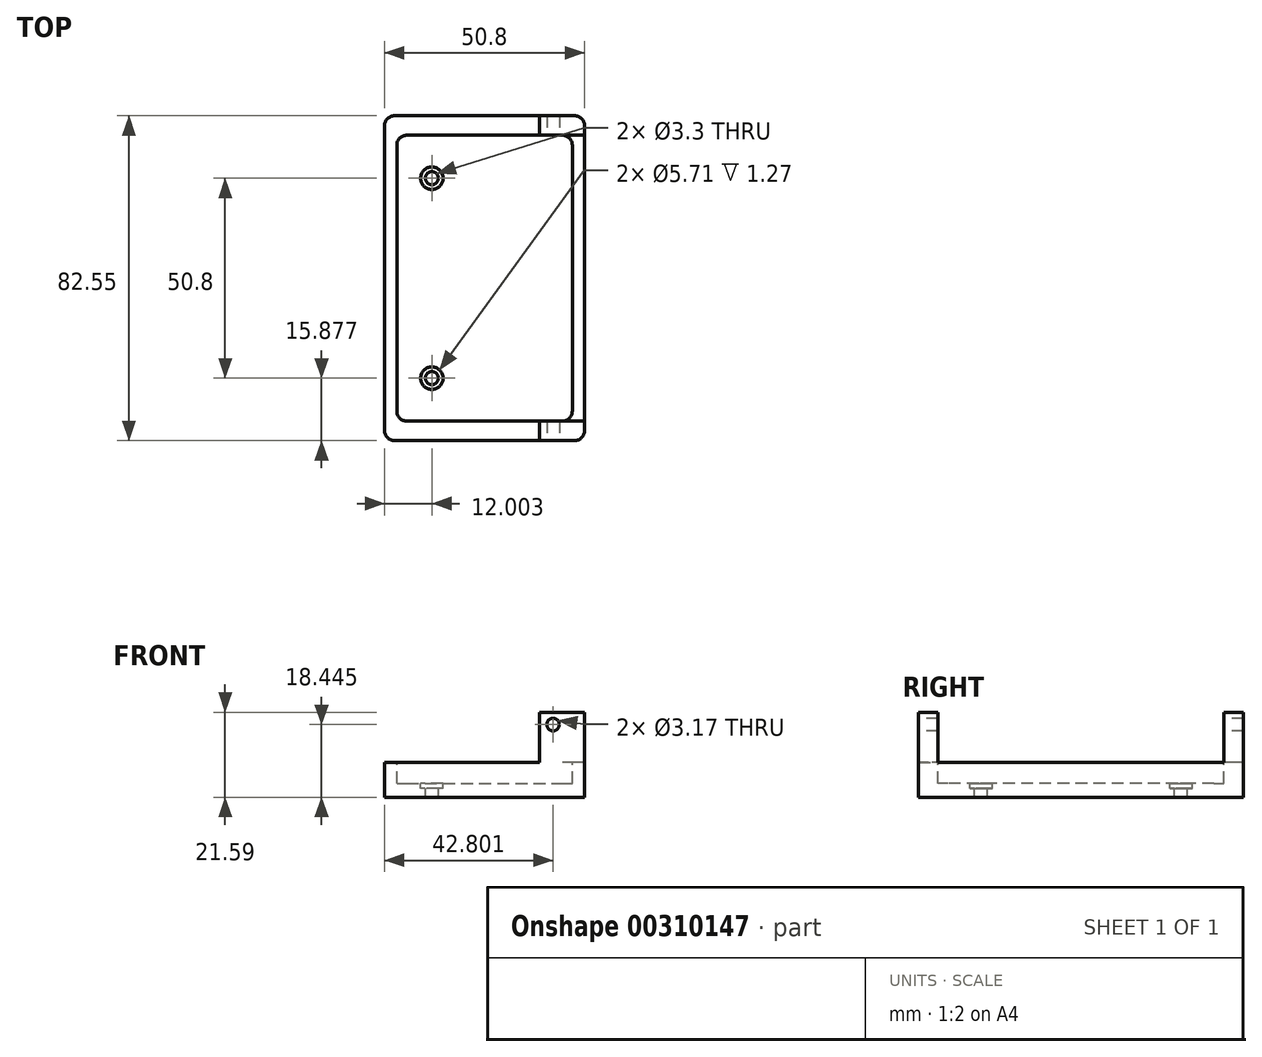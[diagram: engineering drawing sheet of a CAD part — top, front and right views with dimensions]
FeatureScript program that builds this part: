
annotation { "Feature Type Name" : "Feature", "Feature Type Description" : "" }
export const myFeature = defineFeature(function(context is Context, id is Id, definition is map)
    precondition{}
    {
        {
            var Q0;
            Q0=qCreatedBy(makeId("Top.planeOp"),FACE);
            var sketch = newSketch(context, id + "F0", { "sketchPlane" : qUnion([Q0])});
            skLineSegment(sketch, "E0.bottom", {"start": v(-30.54, 37.41) * mm, "end": v(20.26, 37.41) * mm});
            skLineSegment(sketch, "E0.top", {"start": v(-30.54, -45.14) * mm, "end": v(20.26, -45.14) * mm});
            skLineSegment(sketch, "E0.left", {"start": v(-30.54, 37.41) * mm, "end": v(-30.54, -45.14) * mm});
            skLineSegment(sketch, "E0.right", {"start": v(20.26, 37.41) * mm, "end": v(20.26, -45.14) * mm});
            skSolve(sketch);
        }
        {
            var Q0;
            Q0=makeQuery(id+"F0.imprint","IMPRINT",FACE,{"disambiguationData":[TD([[makeQuery(id+"F0.imprint","IMPRINT",EDGE,{"derivedFrom":sQuery(id+"F0.wireOp",EDGE,"E0.bottom")}),-1.0]])]});
            extrude(context, id + "F1", {"entities" : qUnion([Q0]), "depth" : 8.9 * mm});
        }
        {
            var Q0;
            Q0=makeQuery(id+"F1.opExtrude","CAP_FACE",FACE,{"disambiguationData":[OSD([sQuery(id+"F0.wireOp",EDGE,"E0.bottom"),sQuery(id+"F0.wireOp",EDGE,"E0.top"),sQuery(id+"F0.wireOp",EDGE,"E0.left"),sQuery(id+"F0.wireOp",EDGE,"E0.right")])],"isStart":false});
            var sketch = newSketch(context, id + "F2", { "sketchPlane" : qUnion([Q0])});
            skLineSegment(sketch, "E1.bottom", {"start": v(-27.43, 32.46) * mm, "end": v(17.15, 32.46) * mm});
            skLineSegment(sketch, "E1.top", {"start": v(-27.43, -40.19) * mm, "end": v(17.15, -40.19) * mm});
            skLineSegment(sketch, "E1.left", {"start": v(-27.43, 32.46) * mm, "end": v(-27.43, -40.19) * mm});
            skLineSegment(sketch, "E1.right", {"start": v(17.15, 32.46) * mm, "end": v(17.15, -40.19) * mm});
            skSolve(sketch);
        }
        {
            var Q0;
            Q0=makeQuery(id+"F2.imprint","IMPRINT",FACE,{"disambiguationData":[TD([[makeQuery(id+"F2.imprint","IMPRINT",EDGE,{"derivedFrom":sQuery(id+"F2.wireOp",EDGE,"E1.bottom")}),-1.0]])]});
            extrude(context, id + "F3", {"entities" : qUnion([Q0]), "operationType" : NewBodyOperationType.REMOVE, "oppositeDirection" : true, "depth" : 5.33 * mm});
        }
        {
            var Q0;
            Q0=makeQuery(id+"F3.boolean.opBoolean","COPY",EDGE,{"derivedFrom":makeQuery(id+"F3.opExtrude","SWEPT_EDGE",EDGE,{"disambiguationData":[OSD([sQuery(id+"F2.wireOp",EDGE,"E1.bottom"),sQuery(id+"F2.wireOp",EDGE,"E1.left")])]})});
            var Q1;
            Q1=makeQuery(id+"F3.boolean.opBoolean","COPY",EDGE,{"derivedFrom":makeQuery(id+"F3.opExtrude","SWEPT_EDGE",EDGE,{"disambiguationData":[OSD([sQuery(id+"F2.wireOp",EDGE,"E1.bottom"),sQuery(id+"F2.wireOp",EDGE,"E1.right")])]})});
            var Q2;
            Q2=makeQuery(id+"F3.boolean.opBoolean","COPY",EDGE,{"derivedFrom":makeQuery(id+"F3.opExtrude","SWEPT_EDGE",EDGE,{"disambiguationData":[OSD([sQuery(id+"F2.wireOp",EDGE,"E1.top"),sQuery(id+"F2.wireOp",EDGE,"E1.right")])]})});
            var Q3;
            Q3=makeQuery(id+"F3.boolean.opBoolean","COPY",EDGE,{"derivedFrom":makeQuery(id+"F3.opExtrude","SWEPT_EDGE",EDGE,{"disambiguationData":[OSD([sQuery(id+"F2.wireOp",EDGE,"E1.top"),sQuery(id+"F2.wireOp",EDGE,"E1.left")])]})});
            fillet(context, id + "F4", {"entities" : qUnion([Q0, Q1, Q2, Q3]), "radius" : 2.54 * mm, "tangentPropagation" : true, "allowEdgeOverflow" : false});
        }
        {
            var Q0;
            Q0=makeQuery(id+"F3.boolean.opBoolean","COPY",FACE,{"derivedFrom":makeQuery(id+"F3.opExtrude","CAP_FACE",FACE,{"disambiguationData":[OSD([sQuery(id+"F2.wireOp",EDGE,"E1.bottom"),sQuery(id+"F2.wireOp",EDGE,"E1.top"),sQuery(id+"F2.wireOp",EDGE,"E1.left"),sQuery(id+"F2.wireOp",EDGE,"E1.right")])],"isStart":false})});
            var sketch = newSketch(context, id + "F5", { "sketchPlane" : qUnion([Q0])});
            skCircle(sketch, "E2", {"center": v(-18.54, 21.54) * mm, "radius": 1.65 * mm});
            skCircle(sketch, "E3", {"center": v(-18.54, -29.26) * mm, "radius": 1.65 * mm});
            skSolve(sketch);
        }
        {
            var Q0;
            Q0=makeQuery(id+"F5.imprint","IMPRINT",FACE,{"disambiguationData":[TD([[makeQuery(id+"F5.imprint","IMPRINT",EDGE,{"derivedFrom":sQuery(id+"F5.wireOp",EDGE,"E2")}),1.0]])]});
            var Q1;
            Q1=makeQuery(id+"F5.imprint","IMPRINT",FACE,{"disambiguationData":[TD([[makeQuery(id+"F5.imprint","IMPRINT",EDGE,{"derivedFrom":sQuery(id+"F5.wireOp",EDGE,"E3")}),1.0]])]});
            extrude(context, id + "F6", {"entities" : qUnion([Q0, Q1]), "operationType" : NewBodyOperationType.REMOVE, "oppositeDirection" : true, "depth" : 25.4 * mm});
        }
        {
            var Q0;
            Q0=makeQuery(id+"F3.boolean.opBoolean","COPY",FACE,{"derivedFrom":makeQuery(id+"F3.opExtrude","CAP_FACE",FACE,{"disambiguationData":[OSD([sQuery(id+"F2.wireOp",EDGE,"E1.bottom"),sQuery(id+"F2.wireOp",EDGE,"E1.top"),sQuery(id+"F2.wireOp",EDGE,"E1.left"),sQuery(id+"F2.wireOp",EDGE,"E1.right")])],"isStart":false})});
            var sketch = newSketch(context, id + "F7", { "sketchPlane" : qUnion([Q0])});
            skCircle(sketch, "E4", {"center": v(-18.54, 21.54) * mm, "radius": 2.86 * mm});
            skCircle(sketch, "E5", {"center": v(-18.54, -29.26) * mm, "radius": 2.86 * mm});
            skSolve(sketch);
        }
        {
            var Q0;
            Q0 = qSketchRegion(id + "F7", true);
            extrude(context, id + "F8", {"entities" : qUnion([Q0]), "operationType" : NewBodyOperationType.REMOVE, "oppositeDirection" : true, "depth" : 1.27 * mm});
        }
        {
            var Q0;
            Q0=makeQuery(id+"F1.opExtrude","CAP_FACE",FACE,{"disambiguationData":[OSD([sQuery(id+"F0.wireOp",EDGE,"E0.bottom"),sQuery(id+"F0.wireOp",EDGE,"E0.top"),sQuery(id+"F0.wireOp",EDGE,"E0.left"),sQuery(id+"F0.wireOp",EDGE,"E0.right")])],"isStart":false});
            var sketch = newSketch(context, id + "F9", { "sketchPlane" : qUnion([Q0])});
            skLineSegment(sketch, "E6.bottom", {"start": v(20.26, -45.14) * mm, "end": v(8.83, -45.14) * mm});
            skLineSegment(sketch, "E6.top", {"start": v(20.26, -40.19) * mm, "end": v(8.83, -40.19) * mm});
            skLineSegment(sketch, "E6.left", {"start": v(20.26, -45.14) * mm, "end": v(20.26, -40.19) * mm});
            skLineSegment(sketch, "E6.right", {"start": v(8.83, -45.14) * mm, "end": v(8.83, -40.19) * mm});
            skLineSegment(sketch, "E7.bottom", {"start": v(20.26, 37.41) * mm, "end": v(8.83, 37.41) * mm});
            skLineSegment(sketch, "E7.top", {"start": v(20.26, 32.46) * mm, "end": v(8.83, 32.46) * mm});
            skLineSegment(sketch, "E7.left", {"start": v(20.26, 37.41) * mm, "end": v(20.26, 32.46) * mm});
            skLineSegment(sketch, "E7.right", {"start": v(8.83, 37.41) * mm, "end": v(8.83, 32.46) * mm});
            skSolve(sketch);
        }
        {
            var Q0;
            Q0=makeQuery(id+"F9.imprint","IMPRINT",FACE,{"disambiguationData":[TD([[makeQuery(id+"F9.imprint","IMPRINT",EDGE,{"derivedFrom":sQuery(id+"F9.wireOp",EDGE,"E6.bottom")}),1.0]])]});
            var Q1;
            Q1=makeQuery(id+"F9.imprint","IMPRINT",FACE,{"disambiguationData":[TD([[makeQuery(id+"F9.imprint","IMPRINT",EDGE,{"derivedFrom":sQuery(id+"F9.wireOp",EDGE,"E7.bottom")}),-1.0]])]});
            extrude(context, id + "F10", {"entities" : qUnion([Q0, Q1]), "operationType" : NewBodyOperationType.ADD, "depth" : 12.7 * mm});
        }
        {
            var Q0;
            Q0=makeQuery(id+"F10.boolean.opBoolean","MERGE",FACE,{"derivedFrom":[makeQuery(id+"F1.opExtrude","SWEPT_FACE",FACE,{"disambiguationData":[OSD([sQuery(id+"F0.wireOp",EDGE,"E0.top")])]}),makeQuery(id+"F10.opExtrude","SWEPT_FACE",FACE,{"disambiguationData":[OSD([sQuery(id+"F9.wireOp",EDGE,"E6.bottom")])]})]});
            var sketch = newSketch(context, id + "F11", { "sketchPlane" : qUnion([Q0])});
            skCircle(sketch, "E8", {"center": v(12.26, 18.44) * mm, "radius": 1.59 * mm});
            skSolve(sketch);
        }
        {
            var Q0;
            Q0=makeQuery(id+"F11.imprint","IMPRINT",FACE,{"disambiguationData":[TD([[makeQuery(id+"F11.imprint","IMPRINT",EDGE,{"derivedFrom":sQuery(id+"F11.wireOp",EDGE,"E8")}),1.0]])]});
            extrude(context, id + "F12", {"entities" : qUnion([Q0]), "operationType" : NewBodyOperationType.REMOVE, "oppositeDirection" : true, "depth" : 127 * mm});
        }
        {
            var Q0;
            Q0=makeQuery(id+"F10.boolean.opBoolean","MERGE",EDGE,{"derivedFrom":[makeQuery(id+"F1.opExtrude","SWEPT_EDGE",EDGE,{"disambiguationData":[OSD([sQuery(id+"F0.wireOp",EDGE,"E0.top"),sQuery(id+"F0.wireOp",EDGE,"E0.right")])]}),makeQuery(id+"F10.opExtrude","SWEPT_EDGE",EDGE,{"disambiguationData":[OSD([sQuery(id+"F9.wireOp",EDGE,"E6.bottom"),sQuery(id+"F9.wireOp",EDGE,"E6.left")])]})]});
            var Q1;
            Q1=makeQuery(id+"F1.opExtrude","SWEPT_EDGE",EDGE,{"disambiguationData":[OSD([sQuery(id+"F0.wireOp",EDGE,"E0.top"),sQuery(id+"F0.wireOp",EDGE,"E0.left")])]});
            var Q2;
            Q2=makeQuery(id+"F10.boolean.opBoolean","MERGE",EDGE,{"derivedFrom":[makeQuery(id+"F1.opExtrude","SWEPT_EDGE",EDGE,{"disambiguationData":[OSD([sQuery(id+"F0.wireOp",EDGE,"E0.bottom"),sQuery(id+"F0.wireOp",EDGE,"E0.right")])]}),makeQuery(id+"F10.opExtrude","SWEPT_EDGE",EDGE,{"disambiguationData":[OSD([sQuery(id+"F9.wireOp",EDGE,"E7.bottom"),sQuery(id+"F9.wireOp",EDGE,"E7.left")])]})]});
            var Q3;
            Q3=makeQuery(id+"F1.opExtrude","SWEPT_EDGE",EDGE,{"disambiguationData":[OSD([sQuery(id+"F0.wireOp",EDGE,"E0.bottom"),sQuery(id+"F0.wireOp",EDGE,"E0.left")])]});
            fillet(context, id + "F13", {"entities" : qUnion([Q0, Q1, Q2, Q3]), "radius" : 2.54 * mm, "tangentPropagation" : true, "allowEdgeOverflow" : false});
        }
    });
